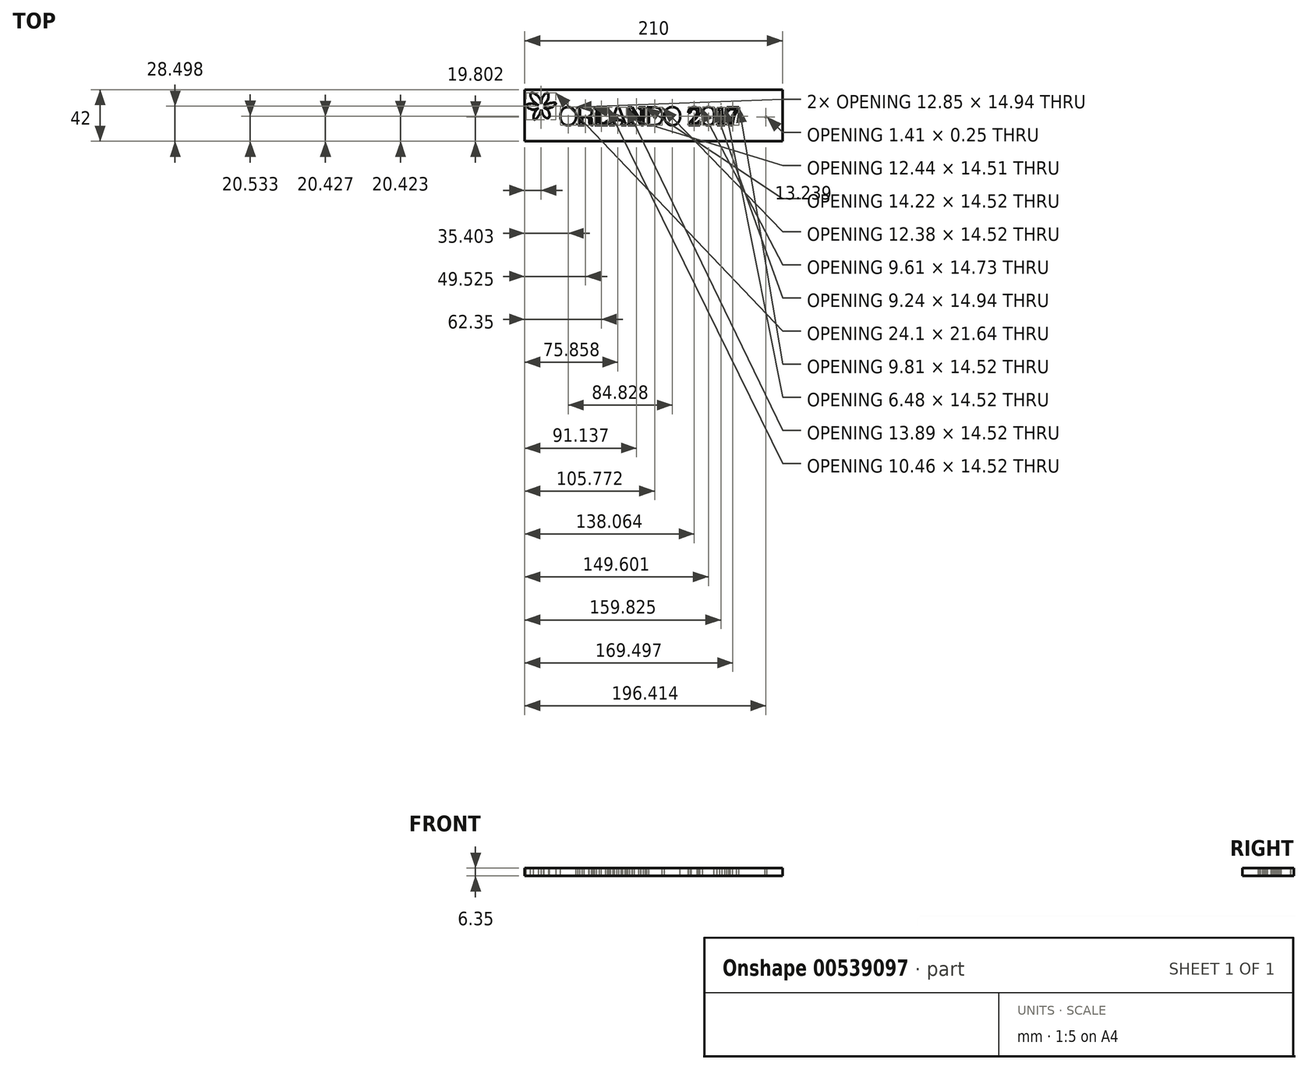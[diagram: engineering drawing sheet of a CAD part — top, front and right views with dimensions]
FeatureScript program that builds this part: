
annotation { "Feature Type Name" : "Feature", "Feature Type Description" : "" }
export const myFeature = defineFeature(function(context is Context, id is Id, definition is map)
    precondition{}
    {
        {
            var Q0;
            Q0=qCreatedBy(makeId("Top.planeOp"),FACE);
            var sketch = newSketch(context, id + "F0", { "sketchPlane" : qUnion([Q0])});
            skLineSegment(sketch, "E0.bottom", {"start": v(105, 21) * mm, "end": v(-105, 21) * mm});
            skLineSegment(sketch, "E0.top", {"start": v(105, -21) * mm, "end": v(-105, -21) * mm});
            skLineSegment(sketch, "E0.left", {"start": v(105, 21) * mm, "end": v(105, -21) * mm});
            skLineSegment(sketch, "E0.right", {"start": v(-105, 21) * mm, "end": v(-105, -21) * mm});
            skPoint(sketch, "E0.middle", {"position": v(0, 0) * mm});
            skText(sketch, "E1", { "text": "ORLANDO 2017\n", "fontName": "RobotoSlab-Regular.ttf"});
            skCircle(sketch, "E2", {"center": v(-91.4, 7.22) * mm, "radius": 2.41 * mm});
            skFitSpline(sketch, "E3", {"points": [v(-91.53, 9.63) * mm, v(-93.64, 15.14) * mm, v(-99.92, 18.29) * mm, v(-99.47, 13.5) * mm, v(-93.56, 8.29) * mm], "startDerivative": vector(-3.22, 23.09) * mm, "endDerivative": vector(24.66, -15.45) * mm});
            skFitSpline(sketch, "E4", {"points": [v(-91.53, 9.63) * mm, v(-90.35, 15.3) * mm, v(-86.46, 18.29) * mm, v(-86.16, 13.5) * mm, v(-89.48, 8.7) * mm], "startDerivative": vector(0.42, 21.85) * mm, "endDerivative": vector(-15.26, -15.6) * mm});
            skFitSpline(sketch, "E5", {"points": [v(-93.56, 8.29) * mm, v(-99.02, 9.72) * mm, v(-103.8, 8.29) * mm, v(-98.87, 4.82) * mm, v(-93.56, 6.16) * mm], "startDerivative": vector(-19.33, 8.05) * mm, "endDerivative": vector(19.18, 10.5) * mm});
            skFitSpline(sketch, "E6", {"points": [v(-93.56, 6.16) * mm, v(-97.08, 1.98) * mm, v(-97.38, -3.4) * mm, v(-93.56, 0) * mm, v(-91.4, 5.29) * mm], "startDerivative": vector(-16.12, -12.79) * mm, "endDerivative": vector(5.45, 19.68) * mm});
            skFitSpline(sketch, "E7", {"points": [v(-91.4, 5.29) * mm, v(-89.75, 0) * mm, v(-86.01, -2.2) * mm, v(-85.72, 3.6) * mm, v(-89.23, 6.16) * mm], "startDerivative": vector(2.75, -20.63) * mm, "endDerivative": vector(-0.45, -0.97) * mm});
            skFitSpline(sketch, "E8", {"points": [v(-89.48, 8.7) * mm, v(-84.52, 10.06) * mm, v(-79.73, 10.06) * mm, v(-84.07, 6.16) * mm, v(-89.2, 6.24) * mm], "startDerivative": vector(16.88, 5.5) * mm, "endDerivative": vector(-14.98, 1.58) * mm});
            skFitSpline(sketch, "E9", {"points": [v(137.72, -16.63) * mm, v(139.65, -9.83) * mm, v(137.47, -3.55) * mm, v(119, 0) * mm, v(118.74, 0) * mm], "startDerivative": vector(8.55, 25.37) * mm, "endDerivative": vector(-2.17, -0.18) * mm});
            skLineSegment(sketch, "E10", {"start": v(120.54, -0.08) * mm, "end": v(122.46, -2.52) * mm});
            skLineSegment(sketch, "E11", {"start": v(122.46, -2.52) * mm, "end": v(122.46, 0) * mm});
            skLineSegment(sketch, "E12", {"start": v(83.99, 0) * mm, "end": v(85.52, -0.38) * mm});
            skLineSegment(sketch, "E13", {"start": v(124, -0.38) * mm, "end": v(124, -2.9) * mm});
            skLineSegment(sketch, "E14", {"start": v(124, -2.9) * mm, "end": v(126.32, -0.65) * mm});
            skLineSegment(sketch, "E15", {"start": v(126.32, -0.65) * mm, "end": v(127.72, -1.11) * mm});
            skLineSegment(sketch, "E16", {"start": v(127.72, -1.11) * mm, "end": v(127.72, -4.7) * mm});
            skLineSegment(sketch, "E17", {"start": v(127.72, -4.7) * mm, "end": v(129.18, -1.07) * mm});
            skLineSegment(sketch, "E18", {"start": v(90.7, -1.07) * mm, "end": v(91.41, -1.2) * mm});
            skLineSegment(sketch, "E19", {"start": v(130.6, -1.33) * mm, "end": v(130.6, -6.5) * mm});
            skLineSegment(sketch, "E20", {"start": v(130.6, -6.5) * mm, "end": v(132.08, -1.64) * mm});
            skLineSegment(sketch, "E21", {"start": v(132.08, -1.64) * mm, "end": v(133.84, -2.09) * mm});
            skLineSegment(sketch, "E22", {"start": v(95.36, -2.09) * mm, "end": v(95.37, -2.1) * mm});
            skLineSegment(sketch, "E23", {"start": v(98.34, -7.84) * mm, "end": v(97.67, -2.88) * mm});
            skLineSegment(sketch, "E24", {"start": v(97.67, -2.88) * mm, "end": v(97.67, -2.88) * mm});
            skLineSegment(sketch, "E25", {"start": v(137.08, -9.83) * mm, "end": v(139.8, -6.9) * mm});
            skLineSegment(sketch, "E26", {"start": v(119, 0) * mm, "end": v(137.72, -16.63) * mm});
            skLineSegment(sketch, "E27", {"start": v(101.33, -6.9) * mm, "end": v(101.33, -6.9) * mm});
            skLineSegment(sketch, "E28", {"start": v(136.15, -2.88) * mm, "end": v(137.08, -9.83) * mm});
            skFitSpline(sketch, "E29", {"points": [v(99.25, -16.63) * mm, v(101.17, -9.83) * mm, v(99, -3.55) * mm, v(80.52, 0) * mm, v(80.27, 0) * mm], "startDerivative": vector(8.55, 25.37) * mm, "endDerivative": vector(-2.17, -0.18) * mm});
            skLineSegment(sketch, "E30", {"start": v(91.41, -1.2) * mm, "end": v(92.12, -1.33) * mm});
            skLineSegment(sketch, "E31", {"start": v(85.52, -0.38) * mm, "end": v(85.52, -0.38) * mm});
            skFitSpline(sketch, "E32", {"points": [v(99.25, -16.63) * mm, v(101.17, -9.83) * mm, v(99, -3.55) * mm, v(80.52, 0) * mm, v(80.27, 0) * mm], "startDerivative": vector(8.55, 25.37) * mm, "endDerivative": vector(-2.17, -0.18) * mm});
            skFitSpline(sketch, "E33.trimOffspring", {"points": [v(137.72, -16.63) * mm, v(139.65, -9.83) * mm, v(137.47, -3.55) * mm, v(119, 0) * mm, v(118.74, 0) * mm], "startDerivative": vector(8.55, 25.37) * mm, "endDerivative": vector(-2.17, -0.18) * mm});
            skLineSegment(sketch, "E34", {"start": v(133.84, -2.1) * mm, "end": v(133.84, -6.8) * mm});
            skLineSegment(sketch, "E35", {"start": v(133.84, -6.8) * mm, "end": v(135.4, -2.1) * mm});
            skLineSegment(sketch, "E36", {"start": v(135.4, -2.1) * mm, "end": v(136.15, -2.88) * mm});
            skPoint(sketch, "E37.startDerivative.orphan", {"position": v(96.92, -17.93) * mm});
            skFitSpline(sketch, "E38.MirrorCS", {"points": [v(137.72, -16.63) * mm, v(131.2, -19.34) * mm, v(124.7, -17.92) * mm, v(119, 0) * mm, v(118.97, 0.25) * mm], "startDerivative": vector(-24.18, -11.48) * mm, "endDerivative": vector(-0.07, 2.18) * mm});
            skLineSegment(sketch, "E39.MirrorCS", {"start": v(130.9, -16.8) * mm, "end": v(128.3, -19.84) * mm});
            skLineSegment(sketch, "E40.MirrorCS", {"start": v(123.88, -16.69) * mm, "end": v(130.9, -16.8) * mm});
            skLineSegment(sketch, "E41.MirrorCS", {"start": v(127.5, -13.94) * mm, "end": v(123.01, -16.03) * mm});
            skLineSegment(sketch, "E42.MirrorCS", {"start": v(122.83, -14.5) * mm, "end": v(127.5, -13.94) * mm});
            skLineSegment(sketch, "E43.MirrorCS", {"start": v(126.82, -10.75) * mm, "end": v(122.17, -12.8) * mm});
            skLineSegment(sketch, "E44.MirrorCS", {"start": v(121.68, -11.36) * mm, "end": v(126.82, -10.75) * mm});
            skLineSegment(sketch, "E45.MirrorCS", {"start": v(124.7, -8.1) * mm, "end": v(121.26, -9.99) * mm});
            skLineSegment(sketch, "E46.MirrorCS", {"start": v(121.13, -8.53) * mm, "end": v(124.7, -8.1) * mm});
            skLineSegment(sketch, "E47.MirrorCS", {"start": v(122.48, -4.62) * mm, "end": v(120.5, -7.2) * mm});
            skLineSegment(sketch, "E48.MirrorCS", {"start": v(119.97, -4.92) * mm, "end": v(122.48, -4.62) * mm});
            skLineSegment(sketch, "E49.MirrorCS", {"start": v(121.91, -3.14) * mm, "end": v(119.4, -3.44) * mm});
            skLineSegment(sketch, "E50.MirrorCS", {"start": v(119.27, -1.52) * mm, "end": v(121.91, -3.14) * mm});
            skFitSpline(sketch, "E51.MirrorCS", {"points": [v(137.72, -16.63) * mm, v(131.2, -19.34) * mm, v(124.7, -17.92) * mm, v(119, 0) * mm, v(118.97, 0.25) * mm], "startDerivative": vector(-24.18, -11.48) * mm, "endDerivative": vector(-0.07, 2.18) * mm});
            skLineSegment(sketch, "E52.MirrorCS", {"start": v(119.4, -3.44) * mm, "end": v(119.97, -4.92) * mm});
            skLineSegment(sketch, "E53.MirrorCS", {"start": v(120.5, -7.2) * mm, "end": v(121.13, -8.53) * mm});
            skFitSpline(sketch, "E54.MirrorCS", {"points": [v(137.72, -16.63) * mm, v(131.2, -19.34) * mm, v(124.7, -17.92) * mm, v(119, 0) * mm, v(118.97, 0.25) * mm], "startDerivative": vector(-24.18, -11.48) * mm, "endDerivative": vector(-0.07, 2.18) * mm});
            skLineSegment(sketch, "E55.MirrorCS", {"start": v(122.17, -12.8) * mm, "end": v(122.82, -14.49) * mm});
            skLineSegment(sketch, "E56.MirrorCS", {"start": v(123.01, -16.03) * mm, "end": v(123.88, -16.69) * mm});
            const initialGuessF0  = {"E1": [-0.07681, -0.00783, 1, 0, 0.0147]};
            skSetInitialGuess(sketch, initialGuessF0);
            skSolve(sketch);
        }
        {
            var Q0;
            Q0=makeQuery(id+"F0.imprint","IMPRINT",FACE,{"disambiguationData":[TD([[makeQuery(id+"F0.imprint","IMPRINT",EDGE,{"derivedFrom":sQuery(id+"F0.wireOp",EDGE,"E0.bottom")}),1.0]])]});
            extrude(context, id + "F1", {"entities" : qUnion([Q0]), "oppositeDirection" : true, "depth" : 6.35 * mm, "offsetDistance" : 25 * mm});
        }
    });
